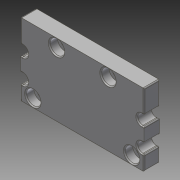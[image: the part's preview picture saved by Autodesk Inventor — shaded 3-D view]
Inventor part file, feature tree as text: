
AUTODESK INVENTOR PART (.ipt)
format: ipt  version: 2014 SP1 (Build 180222100, 222)  size: 216,576 bytes
history: native  units: in
note: dims shown in document units (in); Inventor stores cm internally (conversion verified against a paired STEP export)
features: extrude x2, thread x2, sketch x1, fillet x1, mirror x1
ambient origin geometry x8: Origin, YZ Plane, XZ Plane, XY Plane, X Axis, Y Axis, Z Axis, Center Point
bodies: Solid1 (feature_tree)
feature tree (7):
  sketch  "Sketch1"  dims[d0=0.125in d1=1.75in d4=0.05in d5=1.5in d6=0.375in d7=0.0in d10=0.025in d11=0.475in d12=0.6875in d13=0.35in d14=0.3in d15=0.2in d16=0.2in d17=0.0in d18=0.875in d19=0.2in d20=0.1875in d21=1.0in d22=0.0in d23=1.0in d24=0.0in]
  extrude  "Extrusion1"  Depth=1.75in
  extrude  "Extrusion2"  Depth=0.2in
  fillet  "Fillet1"  Radius=1.5in
  thread  "Thread1"  [1 undecoded]
  thread  "Thread2"  [1 undecoded]
  mirror  "Mirror1"
note: 2 required parameter values undecoded (feature->parameter linkage not recoverable at this tier; creation-order binding heuristic only, values carry confidence <= 0.55)
